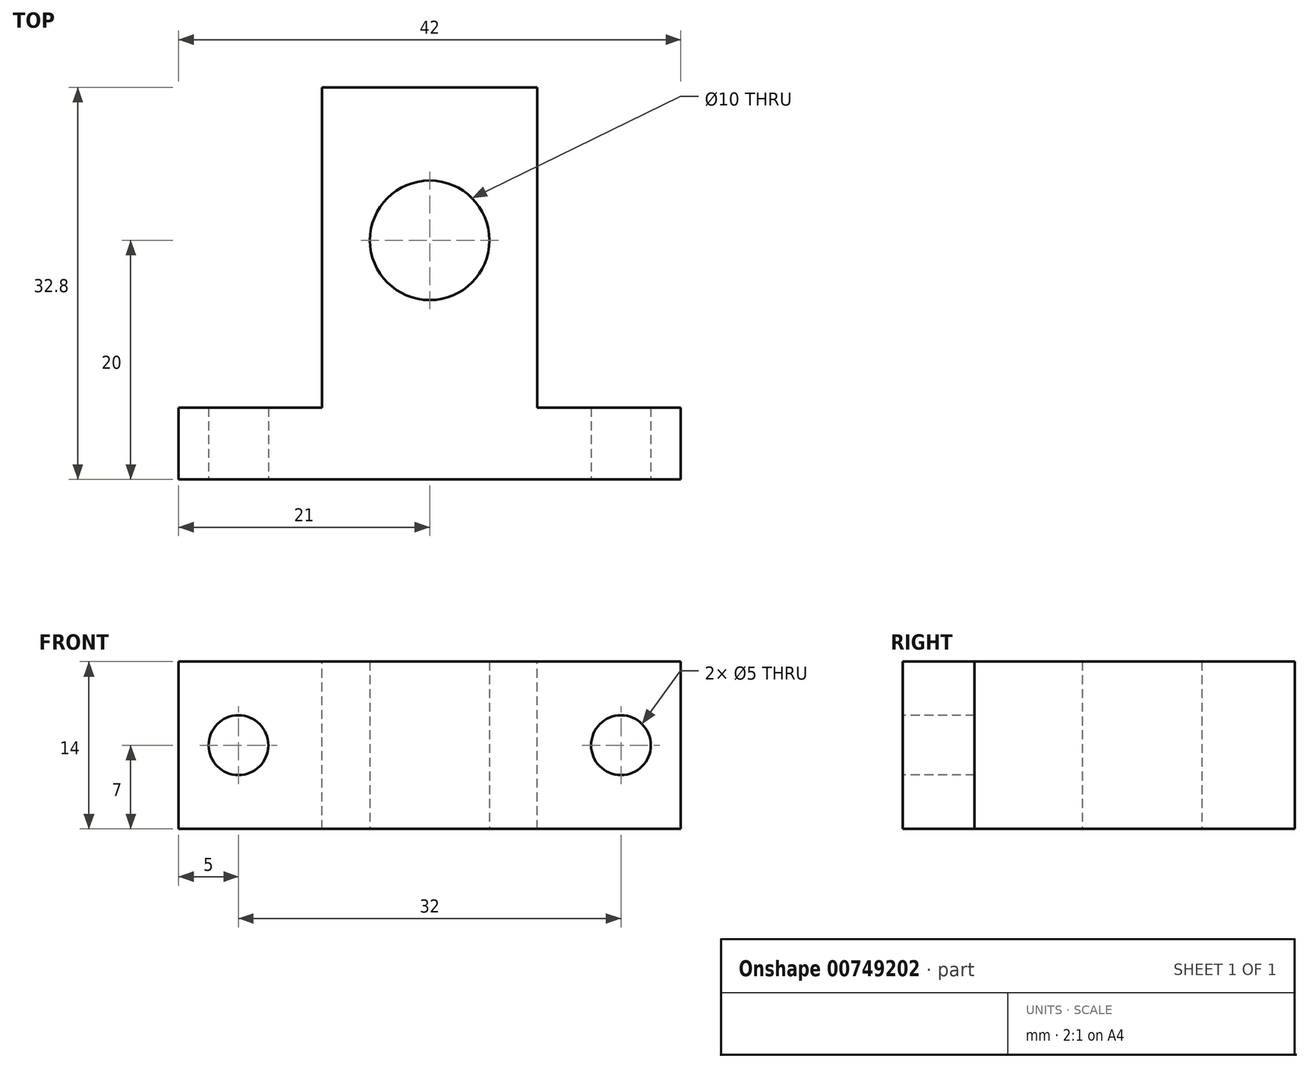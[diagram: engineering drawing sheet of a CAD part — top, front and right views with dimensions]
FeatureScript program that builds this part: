
annotation { "Feature Type Name" : "Feature", "Feature Type Description" : "" }
export const myFeature = defineFeature(function(context is Context, id is Id, definition is map)
    precondition{}
    {
        {
            var Q0;
            Q0=qCreatedBy(makeId("Top.planeOp"),FACE);
            var sketch = newSketch(context, id + "F0", { "sketchPlane" : qUnion([Q0])});
            skLineSegment(sketch, "E0.bottom", {"start": v(0, 0) * mm, "end": v(42, 0) * mm});
            skLineSegment(sketch, "E0.top", {"start": v(0, 32.8) * mm, "end": v(42, 32.8) * mm});
            skLineSegment(sketch, "E0.left", {"start": v(0, 0) * mm, "end": v(0, 32.8) * mm});
            skLineSegment(sketch, "E0.right", {"start": v(42, 0) * mm, "end": v(42, 32.8) * mm});
            skCircle(sketch, "E1", {"center": v(21, 20) * mm, "radius": 5 * mm});
            skSolve(sketch);
        }
        {
            var Q0;
            Q0=qSketchRegion(id+"F0",true);
            extrude(context, id + "F1", {"entities" : qUnion([Q0]), "depth" : 14 * mm});
        }
        {
            var Q0;
            Q0=makeQuery(id+"F1.opExtrude","CAP_FACE",FACE,{"disambiguationData":[OSD([sQuery(id+"F0.wireOp",EDGE,"E0.bottom"),sQuery(id+"F0.wireOp",EDGE,"E0.top"),sQuery(id+"F0.wireOp",EDGE,"E0.left"),sQuery(id+"F0.wireOp",EDGE,"E0.right"),sQuery(id+"F0.wireOp",EDGE,"E1")])],"isStart":false});
            var sketch = newSketch(context, id + "F2", { "sketchPlane" : qUnion([Q0])});
            skLineSegment(sketch, "E2.bottom", {"start": v(0, 32.8) * mm, "end": v(12, 32.8) * mm});
            skLineSegment(sketch, "E2.top", {"start": v(0, 6) * mm, "end": v(12, 6) * mm});
            skLineSegment(sketch, "E2.left", {"start": v(0, 32.8) * mm, "end": v(0, 6) * mm});
            skLineSegment(sketch, "E2.right", {"start": v(12, 32.8) * mm, "end": v(12, 6) * mm});
            skLineSegment(sketch, "E3.bottom", {"start": v(42, 32.8) * mm, "end": v(30, 32.8) * mm});
            skLineSegment(sketch, "E3.top", {"start": v(42, 6) * mm, "end": v(30, 6) * mm});
            skLineSegment(sketch, "E3.left", {"start": v(42, 32.8) * mm, "end": v(42, 6) * mm});
            skLineSegment(sketch, "E3.right", {"start": v(30, 32.8) * mm, "end": v(30, 6) * mm});
            skSolve(sketch);
        }
        {
            var Q0;
            Q0=qSketchRegion(id+"F2",true);
            extrude(context, id + "F3", {"entities" : qUnion([Q0]), "operationType" : NewBodyOperationType.REMOVE, "oppositeDirection" : true, "depth" : 14 * mm});
        }
        {
            var Q0;
            Q0=makeQuery(id+"F1.opExtrude","SWEPT_FACE",FACE,{"disambiguationData":[OSD([sQuery(id+"F0.wireOp",EDGE,"E0.bottom")])]});
            var sketch = newSketch(context, id + "F4", { "sketchPlane" : qUnion([Q0])});
            skCircle(sketch, "E4", {"center": v(5, 7) * mm, "radius": 2.5 * mm});
            skCircle(sketch, "E5", {"center": v(37, 7) * mm, "radius": 2.5 * mm});
            skSolve(sketch);
        }
        {
            var Q0;
            Q0=qSketchRegion(id+"F4",true);
            extrude(context, id + "F5", {"entities" : qUnion([Q0]), "operationType" : NewBodyOperationType.REMOVE, "oppositeDirection" : true, "depth" : 25.4 * mm});
        }
    });
